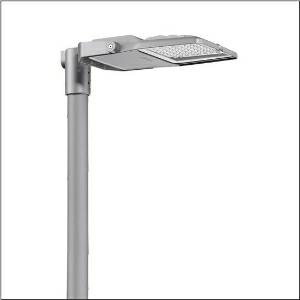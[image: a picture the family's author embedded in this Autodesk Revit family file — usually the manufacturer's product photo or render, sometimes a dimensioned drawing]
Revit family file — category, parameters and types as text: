
# Revit family: floodlight_fl_21_iq_mini___pl64_5xa7772b4e3a_29df
name_source: partatom
category: Lighting Fixtures
units: mm (PartAtom-declared; Revit-internal decimal feet)

## family parameters
Cut with Voids When Loaded = No
Host = Face
Light Source = No
Part Type = Normal
Room Calculation Point = No
Round Connector Dimension = Use Diameter
Shared = No

## types (1)
- --- (1 x LED, 6270 lm, 45.5 W, 4000K)
    Apparent Load = 46 VA
    CIE Flux Codes = 28 80 98 100 100
    Color Rendering = 70
    Color Temperature = 4000K
    Default Elevation = 1800 mm
    Description = Floodlight FL 21 iQ mini, floodlight, primary light control with lens, of PMMA, primary optical cover: protective disc, of toughened safety glass, transparent, light distribution: PL64, light emission: direct distribution, installation type: surface-mounted, lamps: LED, High Power LED, rated values: 6.270lm | 45,5W | 137,8lm/W (begin service life); end service life: 6.270lm | 48W; at 50% lumin. flux: 3.135lm | 21,5W | 145,8lm/W, colour temperature: 4000K, colour rendering: CRI > 70, light colour: 740, light setting 1 begin service life: 100% | 6.270lm | 45,5W | 137,8lm/W | 4.000K, light setting 1 end service life: 48W, further light settings possible, control: Street-Remote, Auto-Match, Temp-Guard, Night-Set, Smart-Wire, Desk-Remote (wireless, voltage-free reading and setting of iQ features in the workshop via application-optimized NFC function/RFID function), optimised constant luminous flux control (CLO 2.0), pre-setting: linear dimming characteristic, with terminal, 6-pole, mains connection: 220..240V, AC, 50/60Hz, luminaire housing, of diecast aluminium, powder-coated, SITECO metallic grey (DB 702S), corrosivity category C5 mid according to DIN EN ISO 12944suitable for swimming poolschlorine-resistant, sealing non-destructively replaceable, please order mast flange separately, mast bracket, of steel, galvanised, powder-coated, protection rating (complete): IP66, insulation class (complete): insulation class II (safety insulation), certification: CE, ENEC, VDE, protection symbol: D, impact resistance: IK08, permissible operating ambient temperature: -40..+40°C, permissible operating ambient temperature for outdoor applications: -40..+50°C, standard: DIN EN 12944, LABS conformity tested according to VDMA 24364:2018-05, packaging unit: 1 piece

Light Distribution: PL64
    Height = 70 mm
    Lamp = 1 x LED
    Lamp Light Flux = 6270 lm
    Lamp Power = 45.5 W
    Lamp count = 1
    Length = 485 mm
    Luminous efficacy = 138 lm/W
    Manufacturer = Siteco
    ModVariant = No
    Model = 5XA7772B4E3A
    Number of Poles = 1
    OnlyDefault = Yes
    Power Factor = 1
    Product Name = Floodlight FL 21 iQ mini | PL64
    Product group = floodlight | pylon annexe
    ProductGroupID = 6201
    Protection Class = Protection class II
    Protection Degree = IP 66
    RLX_Detail_Level = 1
    RLX_Emergency_Light_Flux = 0 lm
    RLX_Emergency_Type = 0
    RLX_Emergency_Type_DB = No
    RlxData = <blob elided: 101549 chars, md5=79b23a7b>
    Socket = socket
    Standby Power = 0 W
    System Light Flux = 6270 lm
    System Power = 46 W
    Type Comments = factory setting: luminous flux: 100 % | dim-lin: 254 | 463 mA
    Type Image = l_1007125.jpg
    URL = http://relux.com
    VarID = @adj_166235
    Voltage = 0 V
    Weight = 0.00 kg
    Width = 337 mm

## geometry (parser evidence)
native form markers: Blend x4, Sweep x11
no freeform markers — native parametric forms only
